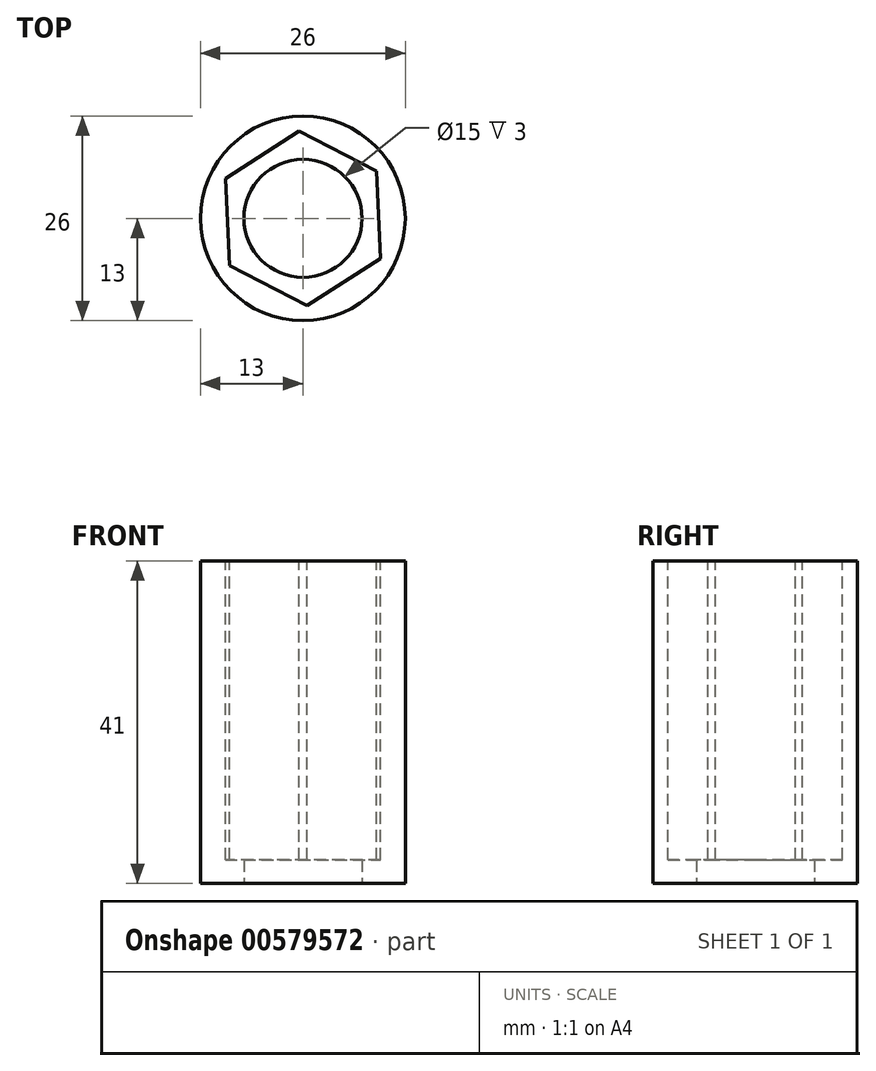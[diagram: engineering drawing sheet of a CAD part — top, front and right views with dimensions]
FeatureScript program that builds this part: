
annotation { "Feature Type Name" : "Feature", "Feature Type Description" : "" }
export const myFeature = defineFeature(function(context is Context, id is Id, definition is map)
    precondition{}
    {
        {
            var Q0;
            Q0=qCreatedBy(makeId("Top.planeOp"),FACE);
            var sketch = newSketch(context, id + "F0", { "sketchPlane" : qUnion([Q0])});
            skCircle(sketch, "E0.cCircle", {"center": v(0, 0) * mm, "radius": 9.6 * mm, "construction": true});
            skLineSegment(sketch, "E0.0", {"start": v(-9.85, 5.08) * mm, "end": v(-0.52, 11.07) * mm});
            skLineSegment(sketch, "E0.1", {"start": v(-0.52, 11.07) * mm, "end": v(9.33, 6) * mm});
            skLineSegment(sketch, "E0.2", {"start": v(9.33, 6) * mm, "end": v(9.85, -5.08) * mm});
            skLineSegment(sketch, "E0.3", {"start": v(9.85, -5.08) * mm, "end": v(0.52, -11.07) * mm});
            skLineSegment(sketch, "E0.4", {"start": v(0.52, -11.07) * mm, "end": v(-9.33, -6) * mm});
            skLineSegment(sketch, "E0.5", {"start": v(-9.33, -6) * mm, "end": v(-9.85, 5.08) * mm});
            skPoint(sketch, "E0.0.midPoint", {"position": v(-5.19, 8.08) * mm});
            skSolve(sketch);
        }
        {
            var Q0;
            Q0=qCreatedBy(makeId("Top.planeOp"),FACE);
            var sketch = newSketch(context, id + "F1", { "sketchPlane" : qUnion([Q0])});
            skCircle(sketch, "E1", {"center": v(0, 0) * mm, "radius": 13 * mm});
            skSolve(sketch);
        }
        {
            var Q0;
            Q0=makeQuery(id+"F1.imprint","IMPRINT",FACE,{"disambiguationData":[TD([[makeQuery(id+"F1.imprint","IMPRINT",EDGE,{"derivedFrom":sQuery(id+"F1.wireOp",EDGE,"E1")}),1.0]])]});
            extrude(context, id + "F2", {"entities" : qUnion([Q0]), "oppositeDirection" : true, "depth" : 41 * mm});
        }
        {
            var Q0;
            Q0=makeQuery(id+"F0.imprint","IMPRINT",FACE,{"disambiguationData":[TD([[makeQuery(id+"F0.imprint","IMPRINT",EDGE,{"derivedFrom":sQuery(id+"F0.wireOp",EDGE,"E0.0")}),-1.0]])]});
            extrude(context, id + "F3", {"entities" : qUnion([Q0]), "operationType" : NewBodyOperationType.REMOVE, "oppositeDirection" : true, "depth" : 38 * mm});
        }
        {
            var Q0;
            Q0=makeQuery(id+"F2.opExtrude","CAP_FACE",FACE,{"disambiguationData":[OSD([sQuery(id+"F1.wireOp",EDGE,"E1")])],"isStart":false});
            var sketch = newSketch(context, id + "F4", { "sketchPlane" : qUnion([Q0])});
            skCircle(sketch, "E2", {"center": v(0, 0) * mm, "radius": 7.5 * mm});
            skSolve(sketch);
        }
        {
            var Q0;
            Q0=makeQuery(id+"F4.imprint","IMPRINT",FACE,{"disambiguationData":[TD([[makeQuery(id+"F4.imprint","IMPRINT",EDGE,{"derivedFrom":sQuery(id+"F4.wireOp",EDGE,"E2")}),1.0]])]});
            extrude(context, id + "F5", {"entities" : qUnion([Q0]), "operationType" : NewBodyOperationType.REMOVE, "oppositeDirection" : true, "depth" : 25 * mm});
        }
    });
